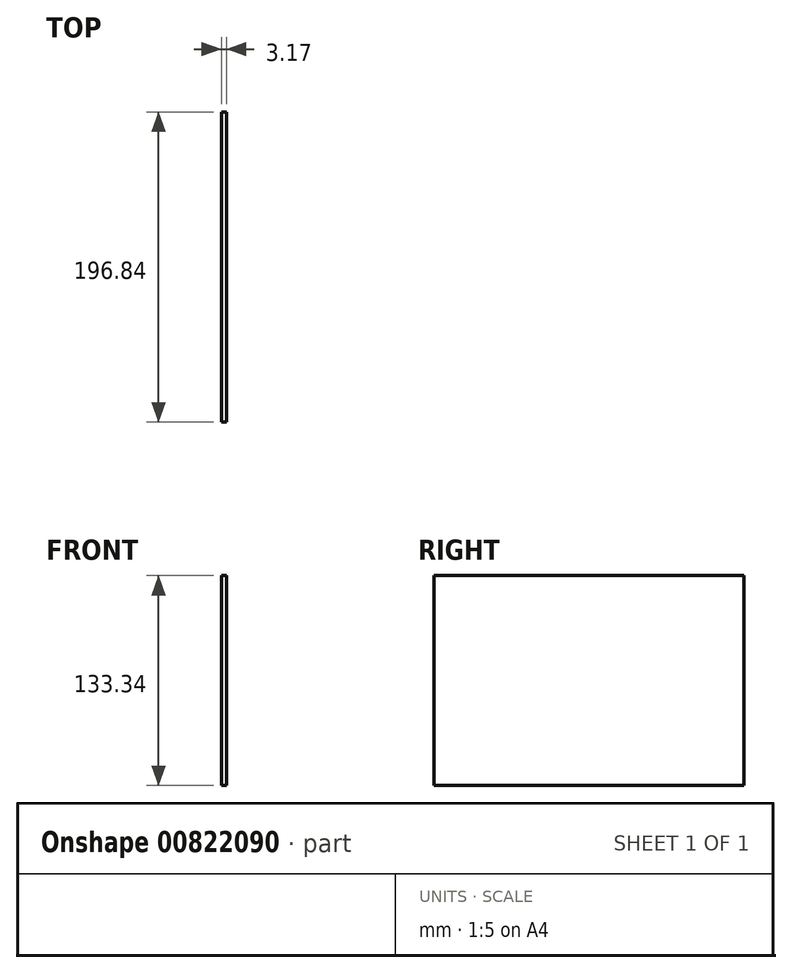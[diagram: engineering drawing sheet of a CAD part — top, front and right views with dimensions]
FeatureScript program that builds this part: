
annotation { "Feature Type Name" : "Feature", "Feature Type Description" : "" }
export const myFeature = defineFeature(function(context is Context, id is Id, definition is map)
    precondition{}
    {
        {
            var Q0;
            Q0=qCreatedBy(makeId("Right.planeOp"),FACE);
            var sketch = newSketch(context, id + "F0", { "sketchPlane" : qUnion([Q0])});
            skLineSegment(sketch, "E0.bottom", {"start": v(-98.42, -66.68) * mm, "end": v(98.43, -66.68) * mm});
            skLineSegment(sketch, "E0.top", {"start": v(-98.43, 66.68) * mm, "end": v(98.42, 66.68) * mm});
            skLineSegment(sketch, "E0.left", {"start": v(-98.42, -66.68) * mm, "end": v(-98.43, 66.68) * mm});
            skLineSegment(sketch, "E0.right", {"start": v(98.43, -66.68) * mm, "end": v(98.42, 66.68) * mm});
            skPoint(sketch, "E0.middle", {"position": v(0, 0) * mm});
            skSolve(sketch);
        }
        {
            var Q0;
            Q0=makeQuery(id+"F0.imprint","IMPRINT",FACE,{"disambiguationData":[TD([[makeQuery(id+"F0.imprint","IMPRINT",EDGE,{"derivedFrom":sQuery(id+"F0.wireOp",EDGE,"E0.bottom")}),1.0]])]});
            extrude(context, id + "F1", {"entities" : qUnion([Q0]), "depth" : 3.17 * mm, "offsetDistance" : 25.4 * mm});
        }
    });
